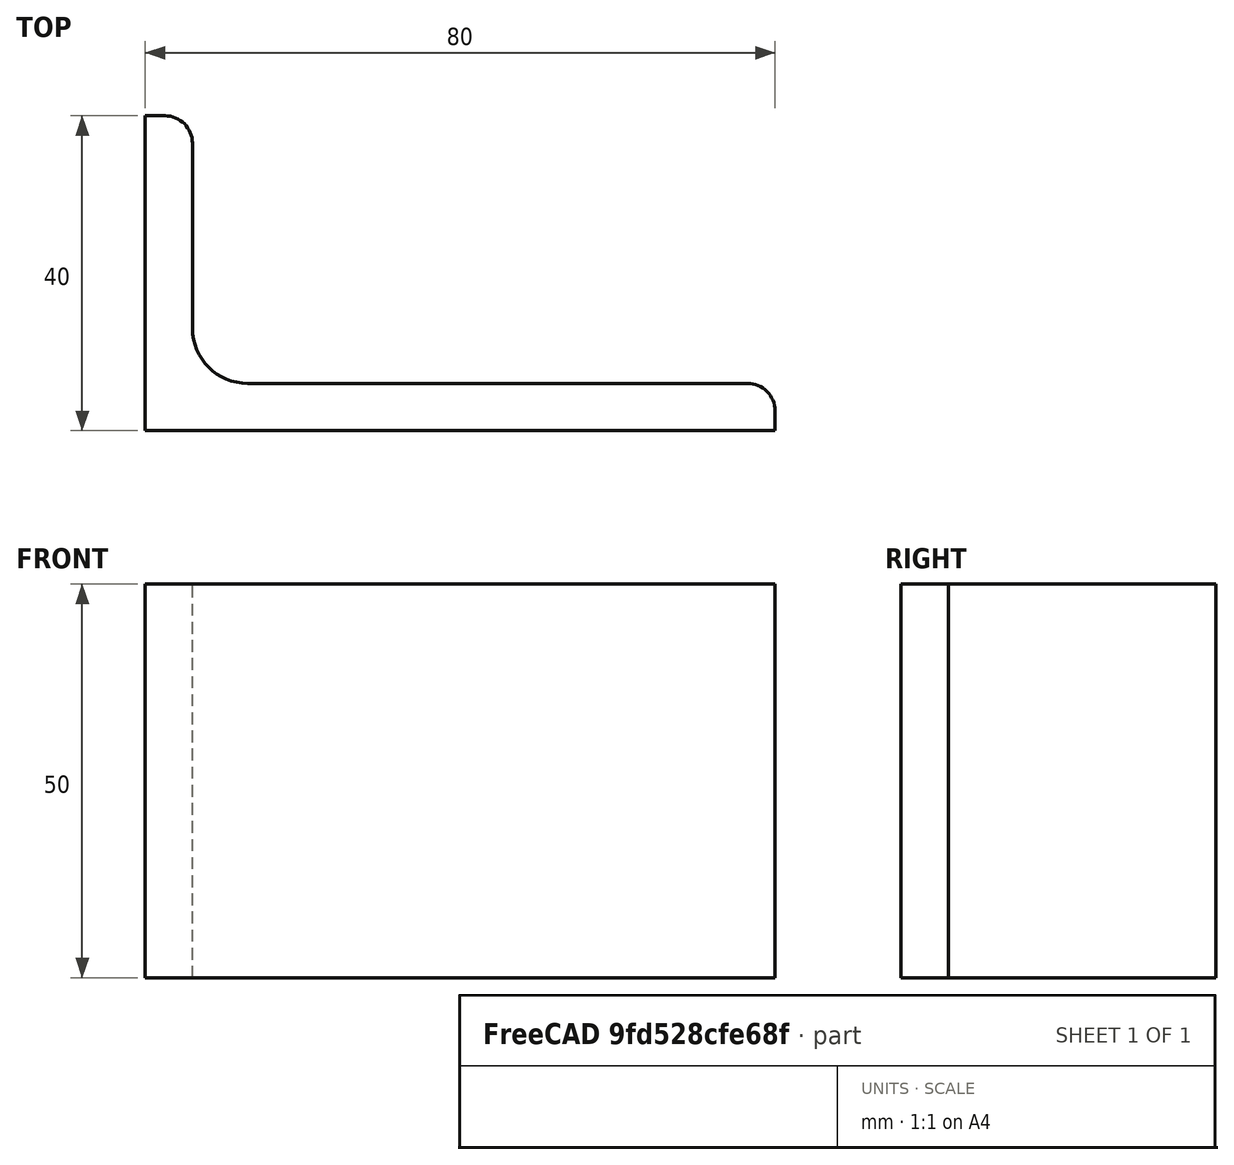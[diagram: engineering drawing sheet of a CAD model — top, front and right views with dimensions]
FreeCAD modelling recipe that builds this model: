
FCSTD DOCUMENT  (FreeCAD 0.15R4671 (Git))
Label: Angle Bar 80x40x6 EN10056 S235JR
License: All rights reserved
LicenseURL: http://en.wikipedia.org/wiki/All_rights_reserved
objects: Sketcher::SketchObject×1, Part::Extrusion×1
note: 2 computed .brp shape members not serialized (recipe doc carries the construction recipe); baked Part::Feature solids carry a one-line shape summary decoded from their .brp

FEATURE [Sketcher::SketchObject] Sketch
  sketch-geometry (9):
    g0: LineSegment StartX=0 StartY=0 StartZ=0 EndX=80 EndY=0 EndZ=0
    g1: LineSegment StartX=80 StartY=0 StartZ=0 EndX=80 EndY=2.5 EndZ=0
    g2: LineSegment StartX=76.5 StartY=6 StartZ=0 EndX=13 EndY=6 EndZ=0
    g3: LineSegment StartX=0 StartY=0 StartZ=0 EndX=0 EndY=40 EndZ=0
    g4: LineSegment StartX=0 StartY=40 StartZ=0 EndX=2.5 EndY=40 EndZ=0
    g5: LineSegment StartX=6 StartY=36.5 StartZ=0 EndX=6 EndY=13 EndZ=0
    g6: ArcOfCircle CenterX=13 CenterY=13 CenterZ=0 NormalX=0 NormalY=0 NormalZ=1 Radius=7 StartAngle=3.14159 EndAngle=4.71239
    g7: ArcOfCircle CenterX=2.5 CenterY=36.5 CenterZ=0 NormalX=0 NormalY=0 NormalZ=1 Radius=3.5 StartAngle=0 EndAngle=1.5708
    g8: ArcOfCircle CenterX=76.5 CenterY=2.5 CenterZ=0 NormalX=0 NormalY=0 NormalZ=1 Radius=3.5 StartAngle=0 EndAngle=1.5708
  constraints (23):
    c: Coincident(g0,g-1)
    c: Horizontal(g0)
    c: Coincident(g1,g0)
    c: Vertical(g1)
    c: Horizontal(g2)
    c: Coincident(g3,g-1)
    c: Vertical(g3)
    c: Coincident(g4,g3)
    c: Horizontal(g4)
    c: Vertical(g5)
    c: Tangent(g5,g6) = -1.5708
    c: Tangent(g2,g6) = 1.5708
    c: Tangent(g4,g7) = 1.5708
    c: Tangent(g5,g7) = 1.5708
    c: Tangent(g2,g8) = -1.5708
    c: Tangent(g1,g8) = -1.5708
    c: DistanceX(g0) = 80
    c: DistanceY(g3) = 40
    c: DistanceY(g0,g2) = 6
    c: DistanceX(g3,g5) = 6
    c: Radius(g6) = 7
    c: Radius(g8) = 3.5
    c: Radius(g7) = 3.5
FEATURE [Part::Extrusion] Extrude  label="Angle Bar 80x40x6 EN10056 S235JR"
  Base = -> Sketch
  Dir = (0,0,50)
  Solid = true
